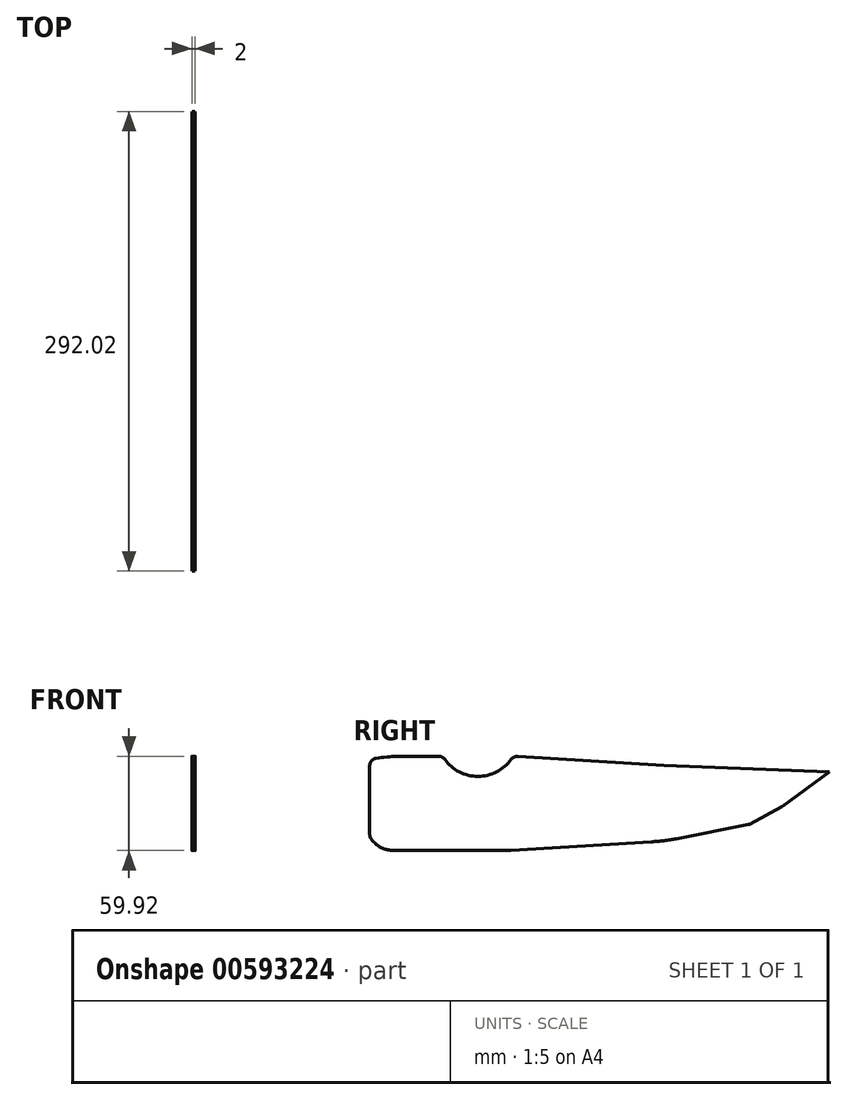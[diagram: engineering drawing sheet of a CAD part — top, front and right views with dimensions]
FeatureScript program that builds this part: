
annotation { "Feature Type Name" : "Feature", "Feature Type Description" : "" }
export const myFeature = defineFeature(function(context is Context, id is Id, definition is map)
    precondition{}
    {
        {
            var Q0;
            Q0=qCreatedBy(makeId("Right.planeOp"),FACE);
            var sketch = newSketch(context, id + "F0", { "sketchPlane" : qUnion([Q0])});
            skLineSegment(sketch, "E0.top", {"start": v(-74.08, -27.74) * mm, "end": v(-3.96, -27.74) * mm});
            skLineSegment(sketch, "E0.left", {"start": v(-93.5, 30) * mm, "end": v(-93.5, -19.17) * mm});
            skPoint(sketch, "E0.middle", {"position": v(0, 2.26) * mm});
            skArc(sketch, "E1", {"start": v(-47.24, 32.26) * mm, "mid": v(-24.74, 19.33) * mm, "end": v(-2.25, 32.26) * mm});
            skFitSpline(sketch, "E2", {"points": [v(-47.24, 32.26) * mm, v(-93.5, 30) * mm], "startDerivative": vector(-46.26, -2.26) * mm, "endDerivative": vector(-44.37, -10.6) * mm});
            skPoint(sketch, "E3.orphan", {"position": v(93.5, 32.26) * mm});
            skLineSegment(sketch, "E4", {"start": v(-3.96, -27.74) * mm, "end": v(93.5, -21.75) * mm});
            skFitSpline(sketch, "E5", {"points": [v(-93.5, -19.17) * mm, v(-74.08, -27.74) * mm], "startDerivative": vector(18.45, -25.72) * mm, "endDerivative": vector(24.51, 0) * mm});
            skPoint(sketch, "E6.orphan", {"position": v(-93.5, -27.74) * mm});
            skLineSegment(sketch, "E7", {"start": v(-2.25, 32.26) * mm, "end": v(93.5, 26.47) * mm});
            skLineSegment(sketch, "E8", {"start": v(93.5, -21.75) * mm, "end": v(147.81, -11.1) * mm});
            skLineSegment(sketch, "E9", {"start": v(147.81, -11.1) * mm, "end": v(168.25, 0) * mm});
            skLineSegment(sketch, "E10", {"start": v(168.25, 0) * mm, "end": v(198.52, 22.15) * mm});
            skLineSegment(sketch, "E11", {"start": v(198.52, 22.15) * mm, "end": v(93.5, 26.47) * mm});
            skSolve(sketch);
        }
        {
            var Q0;
            Q0 = qSketchRegion(id + "F0", true);
            extrude(context, id + "F1", {"entities" : qUnion([Q0]), "depth" : 2 * mm, "offsetDistance" : 25 * mm});
        }
        {
            var Q0;
            Q0=makeQuery(id+"F1.opExtrude","SWEPT_EDGE",EDGE,{"disambiguationData":[OSD([sQuery(id+"F0.wireOp",EDGE,"E0.left"),sQuery(id+"F0.wireOp",EDGE,"E2")])]});
            var Q1;
            Q1=makeQuery(id+"F1.opExtrude","SWEPT_EDGE",EDGE,{"disambiguationData":[OSD([sQuery(id+"F0.wireOp",EDGE,"E0.top"),sQuery(id+"F0.wireOp",EDGE,"E0.left")])]});
            var Q2;
            Q2=makeQuery(id+"F1.opExtrude","SWEPT_EDGE",EDGE,{"disambiguationData":[OSD([sQuery(id+"F0.wireOp",EDGE,"E1"),sQuery(id+"F0.wireOp",EDGE,"E2")])]});
            var Q3;
            Q3=makeQuery(id+"F1.opExtrude","SWEPT_EDGE",EDGE,{"disambiguationData":[OSD([sQuery(id+"F0.wireOp",EDGE,"E0.bottom"),sQuery(id+"F0.wireOp",EDGE,"E1")])]});
            var Q4;
            Q4=makeQuery(id+"F1.opExtrude","SWEPT_EDGE",EDGE,{"disambiguationData":[OSD([sQuery(id+"F0.wireOp",EDGE,"E0.bottom"),sQuery(id+"F0.wireOp",EDGE,"E0.right")])]});
            var Q5;
            Q5=makeQuery(id+"F1.opExtrude","SWEPT_EDGE",EDGE,{"disambiguationData":[OSD([sQuery(id+"F0.wireOp",EDGE,"E0.top"),sQuery(id+"F0.wireOp",EDGE,"E0.right")])]});
            fillet(context, id + "F2", {"entities" : qUnion([Q0, Q1, Q2, Q3, Q4, Q5]), "radius" : 5 * mm, "tangentPropagation" : true, "allowEdgeOverflow" : false});
        }
        {
            var Q0;
            Q0=makeQuery(id+"F1.opExtrude","SWEPT_EDGE",EDGE,{"disambiguationData":[OSD([sQuery(id+"F0.wireOp",EDGE,"E4"),sQuery(id+"F0.wireOp",EDGE,"jm24lxc5-PXpT-eIwz-5dz1-EYjvn02yMdnV")])]});
            fillet(context, id + "F3", {"entities" : qUnion([Q0]), "radius" : 120.7 * mm, "tangentPropagation" : true, "allowEdgeOverflow" : false});
        }
        {
            var Q0;
            Q0=makeQuery(id+"F1.opExtrude","SWEPT_EDGE",EDGE,{"disambiguationData":[OSD([sQuery(id+"F0.wireOp",EDGE,"E8"),sQuery(id+"F0.wireOp",EDGE,"E9")])]});
            var Q1;
            Q1=makeQuery(id+"F1.opExtrude","SWEPT_EDGE",EDGE,{"disambiguationData":[OSD([sQuery(id+"F0.wireOp",EDGE,"E9"),sQuery(id+"F0.wireOp",EDGE,"E10")])]});
            fillet(context, id + "F4", {"entities" : qUnion([Q0, Q1]), "radius" : 4.44 * mm, "tangentPropagation" : true, "allowEdgeOverflow" : false});
        }
    });
